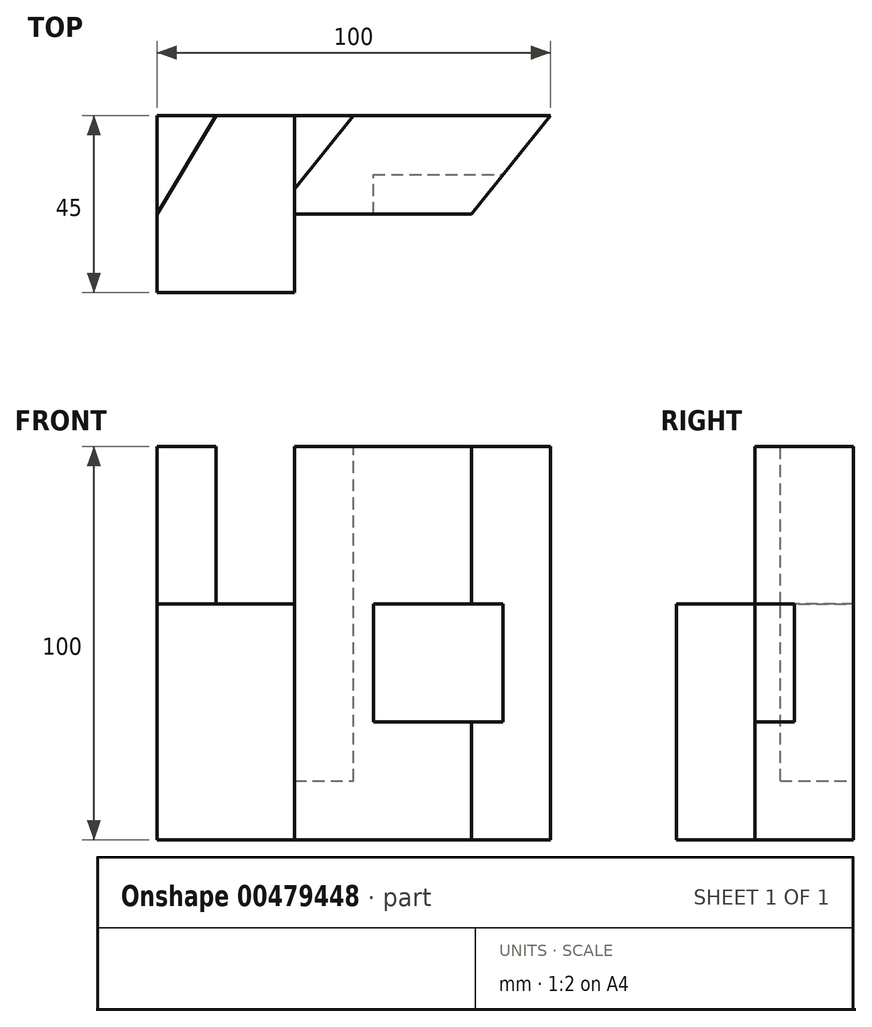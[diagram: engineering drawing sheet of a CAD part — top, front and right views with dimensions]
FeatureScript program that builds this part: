
annotation { "Feature Type Name" : "Feature", "Feature Type Description" : "" }
export const myFeature = defineFeature(function(context is Context, id is Id, definition is map)
    precondition{}
    {
        {
            var Q0;
            Q0=qCreatedBy(makeId("Top.planeOp"),FACE);
            var sketch = newSketch(context, id + "F0", { "sketchPlane" : qUnion([Q0])});
            skLineSegment(sketch, "E0.bottom", {"start": v(0, 0) * mm, "end": v(100, 0) * mm});
            skLineSegment(sketch, "E0.top", {"start": v(0, 45) * mm, "end": v(100, 45) * mm});
            skLineSegment(sketch, "E0.left", {"start": v(0, 0) * mm, "end": v(0, 45) * mm});
            skLineSegment(sketch, "E0.right", {"start": v(100, 0) * mm, "end": v(100, 45) * mm});
            skSolve(sketch);
        }
        {
            var Q0;
            Q0 = qSketchRegion(id + "F0", true);
            extrude(context, id + "F1", {"entities" : qUnion([Q0]), "depth" : 100 * mm});
        }
        {
            var Q0;
            Q0=makeQuery(id+"F1.opExtrude","CAP_FACE",FACE,{"disambiguationData":[OSD([sQuery(id+"F0.wireOp",EDGE,"E0.bottom"),sQuery(id+"F0.wireOp",EDGE,"E0.top"),sQuery(id+"F0.wireOp",EDGE,"E0.left"),sQuery(id+"F0.wireOp",EDGE,"E0.right")])],"isStart":false});
            var sketch = newSketch(context, id + "F2", { "sketchPlane" : qUnion([Q0])});
            skLineSegment(sketch, "E1.bottom", {"start": v(100, 0) * mm, "end": v(35, 0) * mm});
            skLineSegment(sketch, "E1.top", {"start": v(100, 20) * mm, "end": v(35, 20) * mm});
            skLineSegment(sketch, "E1.left", {"start": v(100, 0) * mm, "end": v(100, 20) * mm});
            skLineSegment(sketch, "E1.right", {"start": v(35, 0) * mm, "end": v(35, 20) * mm});
            skSolve(sketch);
        }
        {
            var Q0;
            Q0 = qSketchRegion(id + "F2", true);
            extrude(context, id + "F3", {"entities" : qUnion([Q0]), "operationType" : NewBodyOperationType.REMOVE, "endBound" : BoundingType.THROUGH_ALL, "oppositeDirection" : true, "depth" : 25 * mm});
        }
        {
            var Q0;
            Q0=makeQuery(id+"F1.opExtrude","CAP_FACE",FACE,{"disambiguationData":[OSD([sQuery(id+"F0.wireOp",EDGE,"E0.bottom"),sQuery(id+"F0.wireOp",EDGE,"E0.top"),sQuery(id+"F0.wireOp",EDGE,"E0.left"),sQuery(id+"F0.wireOp",EDGE,"E0.right")])],"isStart":true});
            cPlane(context, id + "F4", {"entities" : qUnion([Q0]), "cplaneType" : CPlaneType.OFFSET, "offset" : 60 * mm, "oppositeDirection" : true, "width" : 150 * mm, "height" : 150 * mm});
        }
        {
            var Q0;
            Q0=makeQuery(id+"F1.opExtrude","CAP_FACE",FACE,{"disambiguationData":[OSD([sQuery(id+"F0.wireOp",EDGE,"E0.bottom"),sQuery(id+"F0.wireOp",EDGE,"E0.top"),sQuery(id+"F0.wireOp",EDGE,"E0.left"),sQuery(id+"F0.wireOp",EDGE,"E0.right")])],"isStart":false});
            var sketch = newSketch(context, id + "F5", { "sketchPlane" : qUnion([Q0])});
            skLineSegment(sketch, "E2", {"start": v(35, 20) * mm, "end": v(35, 0) * mm});
            skLineSegment(sketch, "E3", {"start": v(0, 0) * mm, "end": v(0, 20) * mm});
            skLineSegment(sketch, "E4", {"start": v(35, 20) * mm, "end": v(35, 45) * mm});
            skLineSegment(sketch, "E5", {"start": v(35, 45) * mm, "end": v(15, 45) * mm});
            skLineSegment(sketch, "E6", {"start": v(15, 45) * mm, "end": v(0, 20) * mm});
            skLineSegment(sketch, "E7", {"start": v(0, 0) * mm, "end": v(35, 0) * mm});
            skSolve(sketch);
        }
        {
            var Q0;
            Q0 = qSketchRegion(id + "F5", true);
            var Q1;
            Q1=qCreatedBy(id+"F4.planeOp",FACE);
            extrude(context, id + "F6", {"entities" : qUnion([Q0]), "operationType" : NewBodyOperationType.REMOVE, "endBound" : BoundingType.UP_TO_SURFACE, "oppositeDirection" : true, "endBoundEntityFace" : qUnion([Q1]), "depth" : 40 * mm});
        }
        {
            var Q0;
            Q0=makeQuery(id+"F1.opExtrude","SWEPT_FACE",FACE,{"disambiguationData":[OSD([sQuery(id+"F0.wireOp",EDGE,"E0.right")])]});
            var sketch = newSketch(context, id + "F7", { "sketchPlane" : qUnion([Q0])});
            skLineSegment(sketch, "E8.bottom", {"start": v(20, 30) * mm, "end": v(30, 30) * mm});
            skLineSegment(sketch, "E8.top", {"start": v(20, 60) * mm, "end": v(30, 60) * mm});
            skLineSegment(sketch, "E8.left", {"start": v(20, 30) * mm, "end": v(20, 60) * mm});
            skLineSegment(sketch, "E8.right", {"start": v(30, 30) * mm, "end": v(30, 60) * mm});
            skSolve(sketch);
        }
        {
            var Q0;
            Q0 = qSketchRegion(id + "F7", true);
            extrude(context, id + "F8", {"entities" : qUnion([Q0]), "operationType" : NewBodyOperationType.REMOVE, "oppositeDirection" : true, "depth" : 45 * mm});
        }
        {
            var Q0;
            {var subQ0=sQuery(id+"F0.wireOp",EDGE,"E0.top");var subQ1=sQuery(id+"F0.wireOp",EDGE,"E0.right");Q0=makeQuery(id+"F6.boolean.opBoolean","SPLIT",FACE,{"disambiguationData":[TD([makeQuery(id+"F1.opExtrude","SWEPT_FACE",FACE,{"disambiguationData":[OSD([subQ1])]})])],"derivedFrom":makeQuery(id+"F1.opExtrude","CAP_FACE",FACE,{"disambiguationData":[OSD([sQuery(id+"F0.wireOp",EDGE,"E0.bottom"),subQ0,sQuery(id+"F0.wireOp",EDGE,"E0.left"),subQ1])],"isStart":false})});}
            var sketch = newSketch(context, id + "F9", { "sketchPlane" : qUnion([Q0])});
            skLineSegment(sketch, "E9", {"start": v(100, 45) * mm, "end": v(100, 20) * mm});
            skLineSegment(sketch, "E10", {"start": v(100, 20) * mm, "end": v(80, 20) * mm});
            skLineSegment(sketch, "E11", {"start": v(80, 20) * mm, "end": v(100, 45) * mm});
            skSolve(sketch);
        }
        {
            var Q0;
            Q0 = qSketchRegion(id + "F9", true);
            extrude(context, id + "F10", {"entities" : qUnion([Q0]), "operationType" : NewBodyOperationType.REMOVE, "endBound" : BoundingType.THROUGH_ALL, "oppositeDirection" : true, "depth" : 25 * mm});
        }
        {
            var Q0;
            Q0=makeQuery(id+"F1.opExtrude","CAP_FACE",FACE,{"disambiguationData":[OSD([sQuery(id+"F0.wireOp",EDGE,"E0.bottom"),sQuery(id+"F0.wireOp",EDGE,"E0.top"),sQuery(id+"F0.wireOp",EDGE,"E0.left"),sQuery(id+"F0.wireOp",EDGE,"E0.right")])],"isStart":true});
            cPlane(context, id + "F11", {"entities" : qUnion([Q0]), "cplaneType" : CPlaneType.OFFSET, "offset" : 15 * mm, "oppositeDirection" : true, "width" : 150 * mm, "height" : 150 * mm});
        }
        {
            var Q0;
            {var subQ0=sQuery(id+"F0.wireOp",EDGE,"E0.top");var subQ1=sQuery(id+"F0.wireOp",EDGE,"E0.right");Q0=makeQuery(id+"F6.boolean.opBoolean","SPLIT",FACE,{"disambiguationData":[TD([makeQuery(id+"F1.opExtrude","SWEPT_FACE",FACE,{"disambiguationData":[OSD([subQ1])]})])],"derivedFrom":makeQuery(id+"F1.opExtrude","CAP_FACE",FACE,{"disambiguationData":[OSD([sQuery(id+"F0.wireOp",EDGE,"E0.bottom"),subQ0,sQuery(id+"F0.wireOp",EDGE,"E0.left"),subQ1])],"isStart":false})});}
            var sketch = newSketch(context, id + "F12", { "sketchPlane" : qUnion([Q0])});
            skLineSegment(sketch, "E12", {"start": v(15, 45) * mm, "end": v(50, 45) * mm});
            skLineSegment(sketch, "E13", {"start": v(35, 45) * mm, "end": v(35, 26.4) * mm});
            skLineSegment(sketch, "E14", {"start": v(35, 26.4) * mm, "end": v(50, 45) * mm});
            skSolve(sketch);
        }
        {
            var Q0;
            Q0 = qSketchRegion(id + "F12", true);
            var Q1;
            Q1=qCreatedBy(id+"F11.planeOp",FACE);
            extrude(context, id + "F13", {"entities" : qUnion([Q0]), "operationType" : NewBodyOperationType.REMOVE, "endBound" : BoundingType.UP_TO_SURFACE, "oppositeDirection" : true, "endBoundEntityFace" : qUnion([Q1]), "depth" : 25 * mm});
        }
    });
